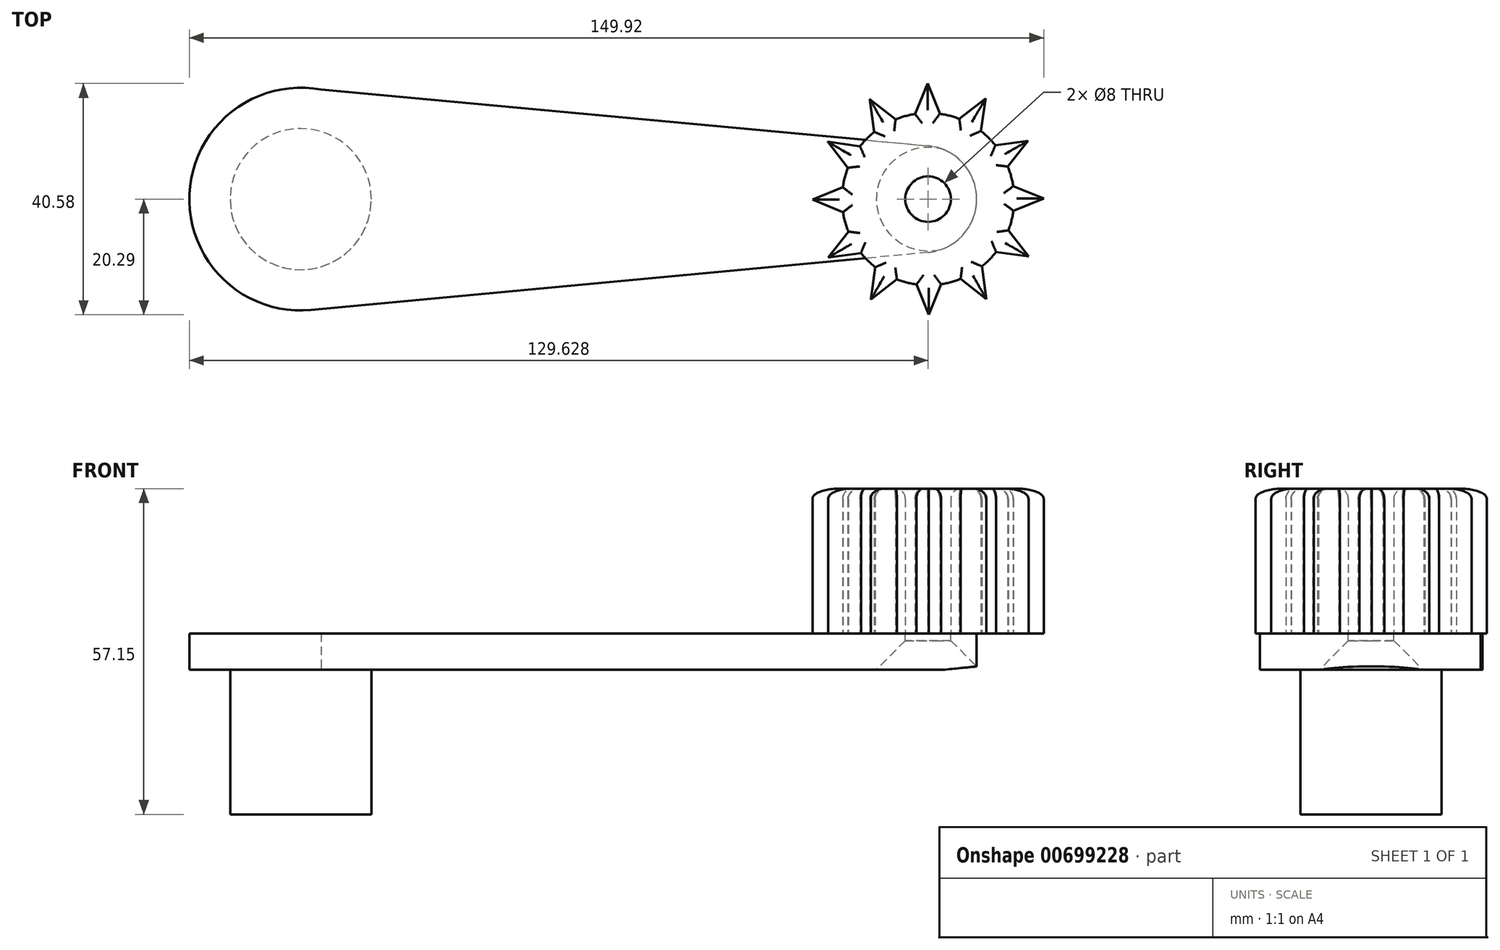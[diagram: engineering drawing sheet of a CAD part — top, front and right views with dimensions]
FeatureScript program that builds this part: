
annotation { "Feature Type Name" : "Feature", "Feature Type Description" : "" }
export const myFeature = defineFeature(function(context is Context, id is Id, definition is map)
    precondition{}
    {
        {
            var Q0;
            Q0=qCreatedBy(makeId("Top.planeOp"),FACE);
            var sketch = newSketch(context, id + "F0", { "sketchPlane" : qUnion([Q0])});
            skArc(sketch, "E0", {"start": v(3.58, 19.2) * mm, "mid": v(-19.52, 0.9) * mm, "end": v(1.81, -19.45) * mm});
            skArc(sketch, "E1", {"start": v(110.09, -9.36) * mm, "mid": v(118.62, 0) * mm, "end": v(110.09, 9.36) * mm});
            skLineSegment(sketch, "E2", {"start": v(0, 19.54) * mm, "end": v(110.09, 9.36) * mm});
            skLineSegment(sketch, "E3", {"start": v(110.09, -9.36) * mm, "end": v(0, -19.62) * mm});
            skSolve(sketch);
        }
        {
            var Q0;
            Q0 = qSketchRegion(id + "F0", true);
            extrude(context, id + "F1", {"entities" : qUnion([Q0]), "depth" : 6.35 * mm, "offsetDistance" : 25.4 * mm});
        }
        {
            var Q0;
            Q0=makeQuery(id+"F1.opExtrude","CAP_FACE",FACE,{"disambiguationData":[OSD([sQuery(id+"F0.wireOp",EDGE,"E0"),sQuery(id+"F0.wireOp",EDGE,"E1"),sQuery(id+"F0.wireOp",EDGE,"E2"),sQuery(id+"F0.wireOp",EDGE,"E3")])],"isStart":false});
            var sketch = newSketch(context, id + "F2", { "sketchPlane" : qUnion([Q0])});
            skCircle(sketch, "E4", {"center": v(110.09, 0) * mm, "radius": 4 * mm});
            skSolve(sketch);
        }
        {
            var Q0;
            Q0 = qSketchRegion(id + "F2", true);
            extrude(context, id + "F3", {"entities" : qUnion([Q0]), "operationType" : NewBodyOperationType.REMOVE, "oppositeDirection" : true, "depth" : 25.4 * mm, "offsetDistance" : 25.4 * mm});
        }
        {
            var Q0;
            Q0=makeQuery(id+"F3.boolean.opBoolean","INTERSECT",EDGE,{"derivedFrom":[makeQuery(id+"F1.opExtrude","CAP_FACE",FACE,{"disambiguationData":[OSD([sQuery(id+"F0.wireOp",EDGE,"E0"),sQuery(id+"F0.wireOp",EDGE,"E1"),sQuery(id+"F0.wireOp",EDGE,"E2"),sQuery(id+"F0.wireOp",EDGE,"E3")])],"isStart":true}),makeQuery(id+"F3.opExtrude","SWEPT_FACE",FACE,{"disambiguationData":[OSD([sQuery(id+"F2.wireOp",EDGE,"E4")])]})]});
            chamfer(context, id + "F4", {"entities" : qUnion([Q0]), "width" : 5.08 * mm, "tangentPropagation" : true});
        }
        {
            var Q0;
            Q0=makeQuery(id+"F1.opExtrude","CAP_FACE",FACE,{"disambiguationData":[OSD([sQuery(id+"F0.wireOp",EDGE,"E0"),sQuery(id+"F0.wireOp",EDGE,"E1"),sQuery(id+"F0.wireOp",EDGE,"E2"),sQuery(id+"F0.wireOp",EDGE,"E3")])],"isStart":true});
            var sketch = newSketch(context, id + "F5", { "sketchPlane" : qUnion([Q0])});
            skCircle(sketch, "E5", {"center": v(0, 0) * mm, "radius": 12.38 * mm});
            skSolve(sketch);
        }
        {
            var Q0;
            Q0 = qSketchRegion(id + "F5", true);
            extrude(context, id + "F6", {"entities" : qUnion([Q0]), "operationType" : NewBodyOperationType.ADD, "depth" : 25.4 * mm, "offsetDistance" : 25.4 * mm});
        }
        {
            var Q0;
            Q0=makeQuery(id+"F1.opExtrude","CAP_FACE",FACE,{"disambiguationData":[OSD([sQuery(id+"F0.wireOp",EDGE,"E0"),sQuery(id+"F0.wireOp",EDGE,"E1"),sQuery(id+"F0.wireOp",EDGE,"E2"),sQuery(id+"F0.wireOp",EDGE,"E3")])],"isStart":false});
            var sketch = newSketch(context, id + "F7", { "sketchPlane" : qUnion([Q0])});
            skCircle(sketch, "E6", {"center": v(110.09, 0) * mm, "radius": 15.1 * mm});
            skLineSegment(sketch, "E7", {"start": v(107.8, 14.93) * mm, "end": v(110, 20.3) * mm});
            skLineSegment(sketch, "E8", {"start": v(110, 20.3) * mm, "end": v(112.14, 14.97) * mm});
            skLineSegment(sketch, "E9.1.0", {"start": v(100.64, 11.79) * mm, "end": v(99.86, 17.53) * mm});
            skLineSegment(sketch, "E9.1.1", {"start": v(99.86, 17.53) * mm, "end": v(104.38, 14) * mm});
            skLineSegment(sketch, "E9.2.0", {"start": v(96, 5.48) * mm, "end": v(92.47, 10.07) * mm});
            skLineSegment(sketch, "E9.2.1", {"start": v(92.47, 10.07) * mm, "end": v(98.15, 9.27) * mm});
            skLineSegment(sketch, "E9.3.0", {"start": v(95.15, -2.3) * mm, "end": v(89.8, -0.09) * mm});
            skLineSegment(sketch, "E9.3.1", {"start": v(89.8, -0.09) * mm, "end": v(95.12, 2.06) * mm});
            skLineSegment(sketch, "E9.4.0", {"start": v(98.3, -9.45) * mm, "end": v(92.56, -10.22) * mm});
            skLineSegment(sketch, "E9.4.1", {"start": v(92.56, -10.22) * mm, "end": v(96.1, -5.7) * mm});
            skLineSegment(sketch, "E9.5.0", {"start": v(104.6, -14.08) * mm, "end": v(100.02, -17.62) * mm});
            skLineSegment(sketch, "E9.5.1", {"start": v(100.02, -17.62) * mm, "end": v(100.82, -11.93) * mm});
            skLineSegment(sketch, "E9.6.0", {"start": v(112.38, -14.93) * mm, "end": v(110.18, -20.3) * mm});
            skLineSegment(sketch, "E9.6.1", {"start": v(110.18, -20.3) * mm, "end": v(108.03, -14.97) * mm});
            skLineSegment(sketch, "E9.7.0", {"start": v(119.54, -11.79) * mm, "end": v(120.31, -17.53) * mm});
            skLineSegment(sketch, "E9.7.1", {"start": v(120.31, -17.53) * mm, "end": v(115.8, -14) * mm});
            skLineSegment(sketch, "E9.8.0", {"start": v(124.17, -5.48) * mm, "end": v(127.7, -10.07) * mm});
            skLineSegment(sketch, "E9.8.1", {"start": v(127.7, -10.07) * mm, "end": v(122.02, -9.27) * mm});
            skLineSegment(sketch, "E9.9.0", {"start": v(125.02, 2.3) * mm, "end": v(130.38, 0.09) * mm});
            skLineSegment(sketch, "E9.9.1", {"start": v(130.38, 0.09) * mm, "end": v(125.06, -2.06) * mm});
            skLineSegment(sketch, "E9.10.0", {"start": v(121.88, 9.45) * mm, "end": v(127.61, 10.22) * mm});
            skLineSegment(sketch, "E9.10.1", {"start": v(127.61, 10.22) * mm, "end": v(124.08, 5.7) * mm});
            skLineSegment(sketch, "E9.11.0", {"start": v(115.57, 14.08) * mm, "end": v(120.16, 17.62) * mm});
            skLineSegment(sketch, "E9.11.1", {"start": v(120.16, 17.62) * mm, "end": v(119.35, 11.93) * mm});
            skCircle(sketch, "E10", {"center": v(110.09, 0) * mm, "radius": 4 * mm});
            skSolve(sketch);
        }
        {
            var Q0;
            Q0 = qSketchRegion(id + "F7", true);
            extrude(context, id + "F8", {"entities" : qUnion([Q0]), "depth" : 25.4 * mm, "offsetDistance" : 25.4 * mm});
        }
        {
            var Q0;
            Q0=makeQuery(id+"F8.opExtrude","CAP_FACE",FACE,{"disambiguationData":[OSD([sQuery(id+"F7.wireOp",EDGE,"E6"),sQuery(id+"F7.wireOp",EDGE,"E7"),sQuery(id+"F7.wireOp",EDGE,"E8"),sQuery(id+"F7.wireOp",EDGE,"E9.1.0"),sQuery(id+"F7.wireOp",EDGE,"E9.1.1"),sQuery(id+"F7.wireOp",EDGE,"E9.2.0"),sQuery(id+"F7.wireOp",EDGE,"E9.2.1"),sQuery(id+"F7.wireOp",EDGE,"E9.3.0"),sQuery(id+"F7.wireOp",EDGE,"E9.3.1"),sQuery(id+"F7.wireOp",EDGE,"E9.4.0"),sQuery(id+"F7.wireOp",EDGE,"E9.4.1"),sQuery(id+"F7.wireOp",EDGE,"E9.5.0"),sQuery(id+"F7.wireOp",EDGE,"E9.5.1"),sQuery(id+"F7.wireOp",EDGE,"E9.6.0"),sQuery(id+"F7.wireOp",EDGE,"E9.6.1"),sQuery(id+"F7.wireOp",EDGE,"E9.7.0"),sQuery(id+"F7.wireOp",EDGE,"E9.7.1"),sQuery(id+"F7.wireOp",EDGE,"E9.8.0"),sQuery(id+"F7.wireOp",EDGE,"E9.8.1"),sQuery(id+"F7.wireOp",EDGE,"E9.9.0"),sQuery(id+"F7.wireOp",EDGE,"E9.9.1"),sQuery(id+"F7.wireOp",EDGE,"E9.10.0"),sQuery(id+"F7.wireOp",EDGE,"E9.10.1"),sQuery(id+"F7.wireOp",EDGE,"E9.11.0"),sQuery(id+"F7.wireOp",EDGE,"E9.11.1")])],"isStart":false});
            fillet(context, id + "F9", {"entities" : qUnion([Q0]), "radius" : 1.78 * mm, "tangentPropagation" : true, "allowEdgeOverflow" : false});
        }
    });
